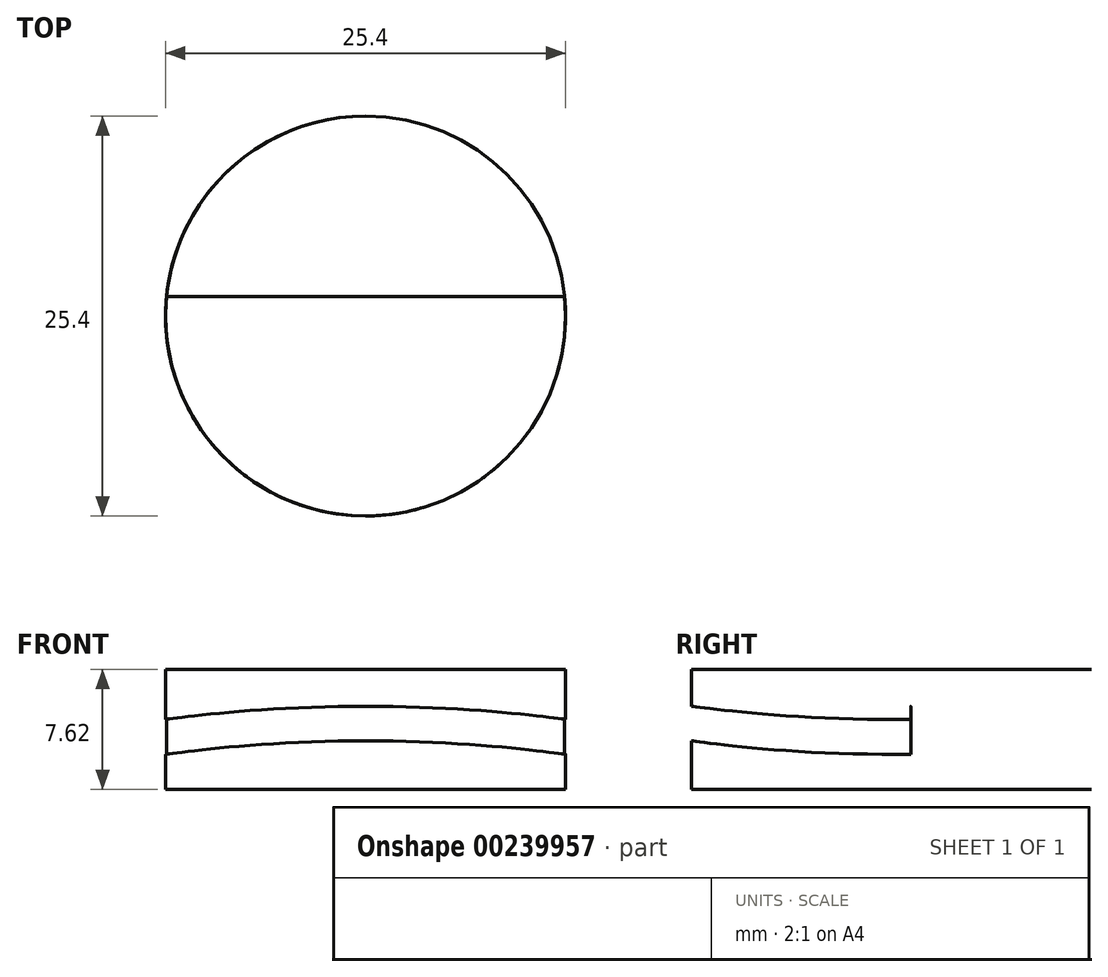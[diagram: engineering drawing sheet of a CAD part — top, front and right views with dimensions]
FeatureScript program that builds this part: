
annotation { "Feature Type Name" : "Feature", "Feature Type Description" : "" }
export const myFeature = defineFeature(function(context is Context, id is Id, definition is map)
    precondition{}
    {
        {
            var Q0;
            Q0=qCreatedBy(makeId("Front.planeOp"),FACE);
            var sketch = newSketch(context, id + "F0", { "sketchPlane" : qUnion([Q0])});
            skCircle(sketch, "E0", {"center": v(0, 0) * mm, "radius": 94.62 * mm});
            skLineSegment(sketch, "E1", {"start": v(-23.95, 91.53) * mm, "end": v(23.95, 91.53) * mm});
            skLineSegment(sketch, "E2", {"start": v(-14.56, 91.53) * mm, "end": v(-14.56, 93.49) * mm});
            skLineSegment(sketch, "E3.MirrorCS", {"start": v(14.56, 91.53) * mm, "end": v(14.56, 93.49) * mm});
            skSolve(sketch);
        }
        {
            var Q0;
            {var subQ0=sQuery(id+"F0.wireOp",EDGE,"E2");Q0=makeQuery(id+"F0.imprint","IMPRINT",FACE,{"disambiguationData":[TD([[makeQuery(id+"F0.imprint","IMPRINT",EDGE,{"derivedFrom":subQ0}),-1.0]])]});}
            extrude(context, id + "F1", {"entities" : qUnion([Q0]), "depth" : 25.4 * mm, "offsetDistance" : 25.4 * mm});
        }
        {
            var Q0;
            Q0=makeQuery(id+"F1.opExtrude","SWEPT_FACE",FACE,{"disambiguationData":[OSD([sQuery(id+"F0.wireOp",EDGE,"E1")])]});
            extrude(context, id + "F2", {"entities" : qUnion([Q0]), "oppositeDirection" : true, "depth" : 7.62 * mm, "offsetDistance" : 25.4 * mm});
        }
        {
            var Q0;
            Q0=makeQuery(id+"F1.opExtrude","SWEPT_BODY",BODY,{"disambiguationData":[OSD([sQuery(id+"F0.wireOp",EDGE,"E0"),sQuery(id+"F0.wireOp",EDGE,"E1"),sQuery(id+"F0.wireOp",EDGE,"E2"),sQuery(id+"F0.wireOp",EDGE,"E3.MirrorCS")])]});
            var Q1;
            Q1=makeQuery(id+"F2.opExtrude","SWEPT_BODY",BODY,{"disambiguationData":[OSD([sQuery(id+"F0.wireOp",EDGE,"E1")])]});
            var Q2;
            Q2=makeQuery(id+"F1.opExtrude","SWEPT_FACE",FACE,{"disambiguationData":[OSD([sQuery(id+"F0.wireOp",EDGE,"E0")])]});
            booleanBodies(context, id + "F3", {"operationType" : BooleanOperationType.SUBTRACTION, "tools" : qUnion([Q0]), "targets" : qUnion([Q1]), "offset" : true, "entitiesToOffset" : qUnion([Q2]), "offsetDistance" : 2.2 * mm, "keepTools" : true});
        }
        {
            var Q0;
            Q0=makeQuery(id+"F2.opExtrude","SWEPT_FACE",FACE,{"disambiguationData":[OSD([sQuery(id+"F0.wireOp",EDGE,"E1"),sQuery(id+"F0.wireOp",EDGE,"E2")])]});
            var sketch = newSketch(context, id + "F4", { "sketchPlane" : qUnion([Q0])});
            skLineSegment(sketch, "E4.bottom", {"start": v(16.55, 99.15) * mm, "end": v(0, 99.15) * mm});
            skLineSegment(sketch, "E4.top", {"start": v(16.55, 91.66) * mm, "end": v(0, 91.66) * mm});
            skLineSegment(sketch, "E4.left", {"start": v(16.55, 99.15) * mm, "end": v(16.55, 91.66) * mm});
            skLineSegment(sketch, "E4.right", {"start": v(0, 99.15) * mm, "end": v(0, 91.66) * mm});
            skSolve(sketch);
        }
        {
            var Q0;
            {var subQ0=sQuery(id+"F4.wireOp",EDGE,"E4.top");Q0=makeQuery(id+"F4.imprint","IMPRINT",FACE,{"disambiguationData":[TD([[makeQuery(id+"F4.imprint","IMPRINT",EDGE,{"derivedFrom":subQ0}),-1.0]])]});}
            var Q1;
            {var subQ0=sQuery(id+"F4.wireOp",EDGE,"E4.bottom");Q1=makeQuery(id+"F4.imprint","IMPRINT",FACE,{"disambiguationData":[TD([[makeQuery(id+"F4.imprint","IMPRINT",EDGE,{"derivedFrom":subQ0}),1.0]])]});}
            var Q2;
            Q2=makeQuery(id+"F2.opExtrude","SWEPT_FACE",FACE,{"disambiguationData":[OSD([sQuery(id+"F0.wireOp",EDGE,"E1"),sQuery(id+"F0.wireOp",EDGE,"E3.MirrorCS")])]});
            extrude(context, id + "F5", {"entities" : qUnion([Q0, Q1]), "operationType" : NewBodyOperationType.ADD, "endBound" : BoundingType.UP_TO_SURFACE, "oppositeDirection" : true, "depth" : 25.4 * mm, "endBoundEntityFace" : qUnion([Q2]), "offsetDistance" : 25.4 * mm});
        }
        {
            var Q0;
            Q0=makeQuery(id+"F2.opExtrude","CAP_FACE",FACE,{"disambiguationData":[OSD([sQuery(id+"F0.wireOp",EDGE,"E1")])],"isStart":false});
            var sketch = newSketch(context, id + "F6", { "sketchPlane" : qUnion([Q0])});
            skCircle(sketch, "E5", {"center": v(0, -12.7) * mm, "radius": 12.7 * mm});
            skPoint(sketch, "E5.centerSnap0", {"position": v(14.56, -12.7) * mm});
            skSolve(sketch);
        }
        {
            var Q0;
            Q0=sQuery(id+"F6.wireOp",VERTEX,"E5.center");
            var Q1;
            Q1=qCreatedBy(makeId("Front.planeOp"),FACE);
            cPlane(context, id + "F7", {"entities" : qUnion([Q0, Q1]), "cplaneType" : CPlaneType.PLANE_POINT, "offset" : 25.4 * mm, "width" : 152.4 * mm, "height" : 152.4 * mm});
        }
        {
            var Q0;
            Q0=qCreatedBy(id+"F7.planeOp",FACE);
            var sketch = newSketch(context, id + "F8", { "sketchPlane" : qUnion([Q0])});
            skFitSpline(sketch, "E6", {"points": [v(-19.88, 136.84) * mm, v(0, 99.13) * mm], "startDerivative": vector(50.37, -31.7) * mm, "endDerivative": vector(0, -37.21) * mm});
            skSolve(sketch);
        }
        {
            var Q0;
            Q0=sQuery(id+"F8.wireOp",VERTEX,"E6.start");
            var Q1;
            Q1=makeQuery(id+"F6.imprint","IMPRINT",FACE,{"disambiguationData":[TD([[makeQuery(id+"F6.imprint","IMPRINT",EDGE,{"derivedFrom":sQuery(id+"F6.wireOp",EDGE,"E5")}),1.0]])]});
            var Q2;
            Q2=sQuery(id+"F8.wireOp",EDGE,"E6");
            loft(context, id + "F9", {"operationType" : NewBodyOperationType.ADD, "sheetProfilesArray" : [{ "sheetProfileEntities" : qUnion([Q0]) }, { "sheetProfileEntities" : qUnion([Q1]) }], "endCondition" : LoftEndDerivativeType.MATCH_CURVATURE, "endMagnitude" : 0.5, "addSections" : true, "spine" : qUnion([Q2]), "sectionCount" : 5});
        }
        {
            var Q0;
            Q0=makeQuery(id+"F5.opExtrude","SWEPT_FACE",FACE,{"disambiguationData":[OSD([sQuery(id+"F4.wireOp",EDGE,"E4.left")])]});
            extrude(context, id + "F10", {"entities" : qUnion([Q0]), "operationType" : NewBodyOperationType.REMOVE, "oppositeDirection" : true, "depth" : 5.08 * mm, "offsetDistance" : 25.4 * mm});
        }
        {
            var Q0;
            Q0=makeQuery(id+"F2.opExtrude","CAP_FACE",FACE,{"disambiguationData":[OSD([sQuery(id+"F0.wireOp",EDGE,"E1")])],"isStart":false});
            extrude(context, id + "F11", {"entities" : qUnion([Q0]), "operationType" : NewBodyOperationType.REMOVE, "oppositeDirection" : true, "depth" : 25.4 * mm, "offsetDistance" : 25.4 * mm});
        }
    });
